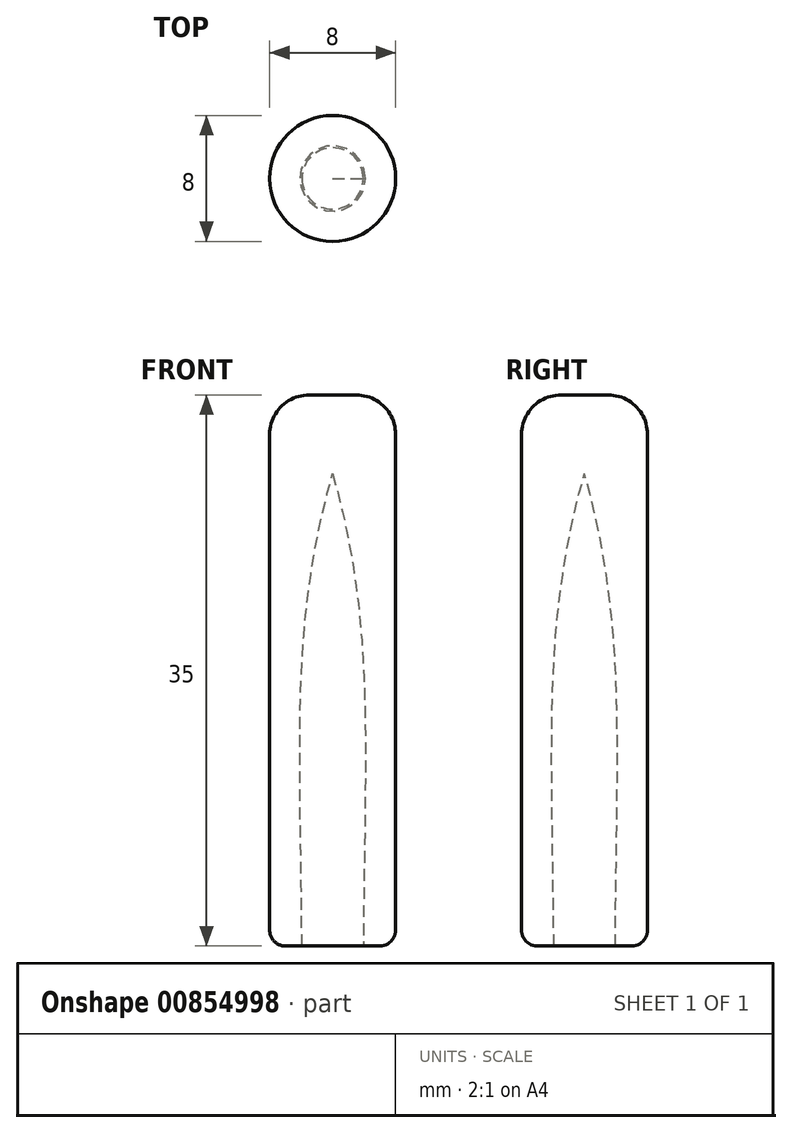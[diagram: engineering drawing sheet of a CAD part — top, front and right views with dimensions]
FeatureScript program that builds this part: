
annotation { "Feature Type Name" : "Feature", "Feature Type Description" : "" }
export const myFeature = defineFeature(function(context is Context, id is Id, definition is map)
    precondition{}
    {
        {
            var Q0;
            Q0=qCreatedBy(makeId("Front.planeOp"),FACE);
            var sketch = newSketch(context, id + "F0", { "sketchPlane" : qUnion([Q0])});
            skLineSegment(sketch, "E0", {"start": v(0, -11.16) * mm, "end": v(4, -11.16) * mm});
            skLineSegment(sketch, "E1", {"start": v(4, -11.16) * mm, "end": v(4, 23.84) * mm});
            skLineSegment(sketch, "E2", {"start": v(4, 23.84) * mm, "end": v(0, 23.84) * mm});
            skLineSegment(sketch, "E3", {"start": v(0, 23.84) * mm, "end": v(0, 18.84) * mm});
            skFitSpline(sketch, "E4", {"points": [v(0, 18.84) * mm, v(1.95, -11.16) * mm], "startDerivative": vector(8, -28.45) * mm, "endDerivative": vector(-0.32, -40) * mm});
            skLineSegment(sketch, "E5", {"start": v(0, -11.16) * mm, "end": v(0, 18.84) * mm, "construction": true});
            skSolve(sketch);
        }
        {
            var Q0;
            {var subQ0=sQuery(id+"F0.wireOp",EDGE,"E1");Q0=makeQuery(id+"F0.imprint","IMPRINT",FACE,{"disambiguationData":[TD([[makeQuery(id+"F0.imprint","IMPRINT",EDGE,{"derivedFrom":subQ0}),1.0]])]});}
            var Q1;
            Q1=sQuery(id+"F0.wireOp",EDGE,"E5");
            revolve(context, id + "F1", {"surfaceOperationType" : NewSurfaceOperationType.NEW, "entities" : qUnion([Q0]), "axis" : qUnion([Q1]), "revolveType" : RevolveType.FULL});
        }
        {
            var Q0;
            Q0=makeQuery(id+"F1.opRevolve","SWEPT_EDGE",EDGE,{"disambiguationData":[OSD([sQuery(id+"F0.wireOp",EDGE,"E1"),sQuery(id+"F0.wireOp",EDGE,"E2")])]});
            fillet(context, id + "F2", {"entities" : qUnion([Q0]), "radius" : 2.5 * mm, "tangentPropagation" : true, "allowEdgeOverflow" : false});
        }
        {
            var Q0;
            Q0=makeQuery(id+"F1.opRevolve","SWEPT_EDGE",EDGE,{"disambiguationData":[OSD([sQuery(id+"F0.wireOp",EDGE,"E0"),sQuery(id+"F0.wireOp",EDGE,"E1")])]});
            fillet(context, id + "F3", {"entities" : qUnion([Q0]), "radius" : 1 * mm, "tangentPropagation" : true, "allowEdgeOverflow" : false});
        }
    });
